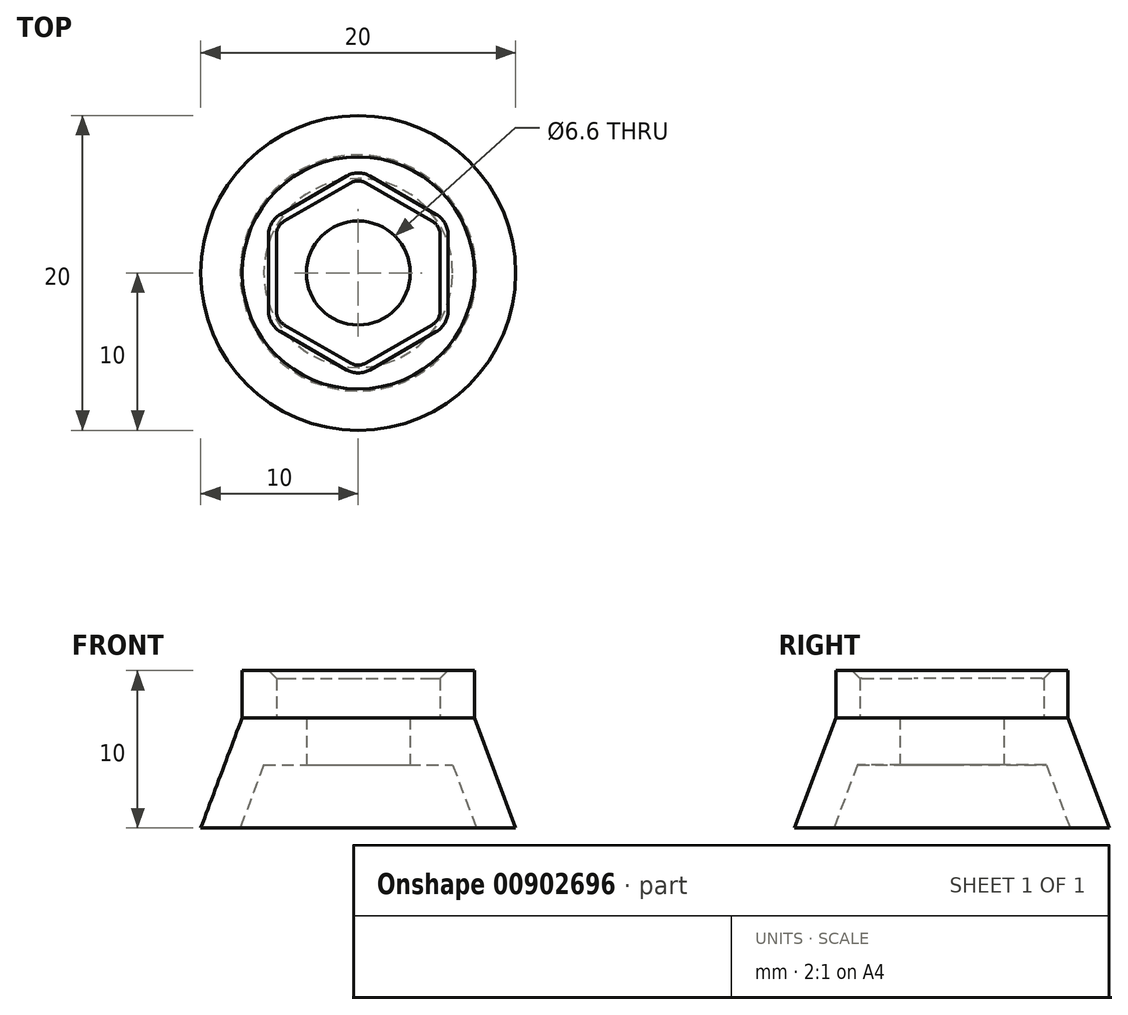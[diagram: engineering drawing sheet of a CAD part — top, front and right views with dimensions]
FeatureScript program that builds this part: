
annotation { "Feature Type Name" : "Feature", "Feature Type Description" : "" }
export const myFeature = defineFeature(function(context is Context, id is Id, definition is map)
    precondition{}
    {
        {
            var Q0;
            Q0=qCreatedBy(makeId("Front.planeOp"),FACE);
            var sketch = newSketch(context, id + "F0", { "sketchPlane" : qUnion([Q0])});
            skLineSegment(sketch, "E0", {"start": v(3.3, 3) * mm, "end": v(7.38, 3) * mm});
            skLineSegment(sketch, "E1", {"start": v(7.38, 3) * mm, "end": v(10, -4) * mm});
            skLineSegment(sketch, "E2", {"start": v(10, -4) * mm, "end": v(7.5, -4) * mm});
            skLineSegment(sketch, "E3", {"start": v(7.5, -4) * mm, "end": v(6, 0) * mm});
            skLineSegment(sketch, "E4", {"start": v(6, 0) * mm, "end": v(3.3, 0) * mm});
            skLineSegment(sketch, "E5", {"start": v(3.3, 0) * mm, "end": v(3.3, 3) * mm});
            skLineSegment(sketch, "E6", {"start": v(0, -7.48) * mm, "end": v(0, 7.13) * mm, "construction": true});
            skSolve(sketch);
        }
        {
            var Q0;
            Q0=makeQuery(id+"F0.imprint","IMPRINT",FACE,{"disambiguationData":[TD([[makeQuery(id+"F0.imprint","IMPRINT",EDGE,{"derivedFrom":sQuery(id+"F0.wireOp",EDGE,"E0")}),-1.0]])]});
            var Q1;
            Q1=sQuery(id+"F0.wireOp",EDGE,"E6");
            revolve(context, id + "F1", {"surfaceOperationType" : NewSurfaceOperationType.NEW, "entities" : qUnion([Q0]), "axis" : qUnion([Q1]), "revolveType" : RevolveType.FULL});
        }
        {
            var Q0;
            Q0=makeQuery(id+"F1.opRevolve","SWEPT_FACE",FACE,{"disambiguationData":[OSD([sQuery(id+"F0.wireOp",EDGE,"E0")])]});
            var sketch = newSketch(context, id + "F2", { "sketchPlane" : qUnion([Q0])});
            skCircle(sketch, "E7.cCircle", {"center": v(0, 0) * mm, "radius": 5.2 * mm, "construction": true});
            skLineSegment(sketch, "E7.0", {"start": v(0.5, 5.72) * mm, "end": v(4.7, 3.3) * mm});
            skLineSegment(sketch, "E7.1", {"start": v(5.2, 2.42) * mm, "end": v(5.2, -2.42) * mm});
            skLineSegment(sketch, "E7.2", {"start": v(4.7, -3.3) * mm, "end": v(0.5, -5.72) * mm});
            skLineSegment(sketch, "E7.3", {"start": v(-0.5, -5.72) * mm, "end": v(-4.7, -3.3) * mm});
            skLineSegment(sketch, "E7.4", {"start": v(-5.2, -2.42) * mm, "end": v(-5.2, 2.42) * mm});
            skLineSegment(sketch, "E7.5", {"start": v(-4.7, 3.3) * mm, "end": v(-0.5, 5.72) * mm});
            skPoint(sketch, "E7.0.midPoint", {"position": v(2.6, 4.5) * mm});
            skCircle(sketch, "E8", {"center": v(0, 0) * mm, "radius": 7.38 * mm});
            skPoint(sketch, "E9.visualSharp", {"position": v(0, 6) * mm});
            skArc(sketch, "E9.filletArc", {"start": v(0.5, 5.72) * mm, "mid": v(0, 5.85) * mm, "end": v(-0.5, 5.72) * mm});
            skPoint(sketch, "E10.visualSharp", {"position": v(5.2, 3) * mm});
            skArc(sketch, "E10.filletArc", {"start": v(5.2, 2.42) * mm, "mid": v(5.07, 2.92) * mm, "end": v(4.7, 3.3) * mm});
            skPoint(sketch, "E11.visualSharp", {"position": v(5.2, -3) * mm});
            skArc(sketch, "E11.filletArc", {"start": v(4.7, -3.3) * mm, "mid": v(5.07, -2.92) * mm, "end": v(5.2, -2.42) * mm});
            skPoint(sketch, "E12.visualSharp", {"position": v(0, -6) * mm});
            skArc(sketch, "E12.filletArc", {"start": v(-0.5, -5.72) * mm, "mid": v(0, -5.85) * mm, "end": v(0.5, -5.72) * mm});
            skPoint(sketch, "E13.visualSharp", {"position": v(-5.2, -3) * mm});
            skArc(sketch, "E13.filletArc", {"start": v(-5.2, -2.42) * mm, "mid": v(-5.07, -2.92) * mm, "end": v(-4.7, -3.3) * mm});
            skPoint(sketch, "E14.visualSharp", {"position": v(-5.2, 3) * mm});
            skArc(sketch, "E14.filletArc", {"start": v(-4.7, 3.3) * mm, "mid": v(-5.07, 2.92) * mm, "end": v(-5.2, 2.42) * mm});
            skSolve(sketch);
        }
        {
            var Q0;
            Q0 = qSketchRegion(id + "F2", true);
            extrude(context, id + "F3", {"entities" : qUnion([Q0]), "operationType" : NewBodyOperationType.ADD, "depth" : 3 * mm, "offsetDistance" : 25 * mm});
        }
        {
            var Q0;
            Q0=makeQuery(id+"F3.opExtrude","CAP_EDGE",EDGE,{"disambiguationData":[OSD([sQuery(id+"F2.wireOp",EDGE,"E7.4")])],"isStart":false});
            chamfer(context, id + "F4", {"entities" : qUnion([Q0]), "width" : 0.5 * mm, "tangentPropagation" : true});
        }
    });
